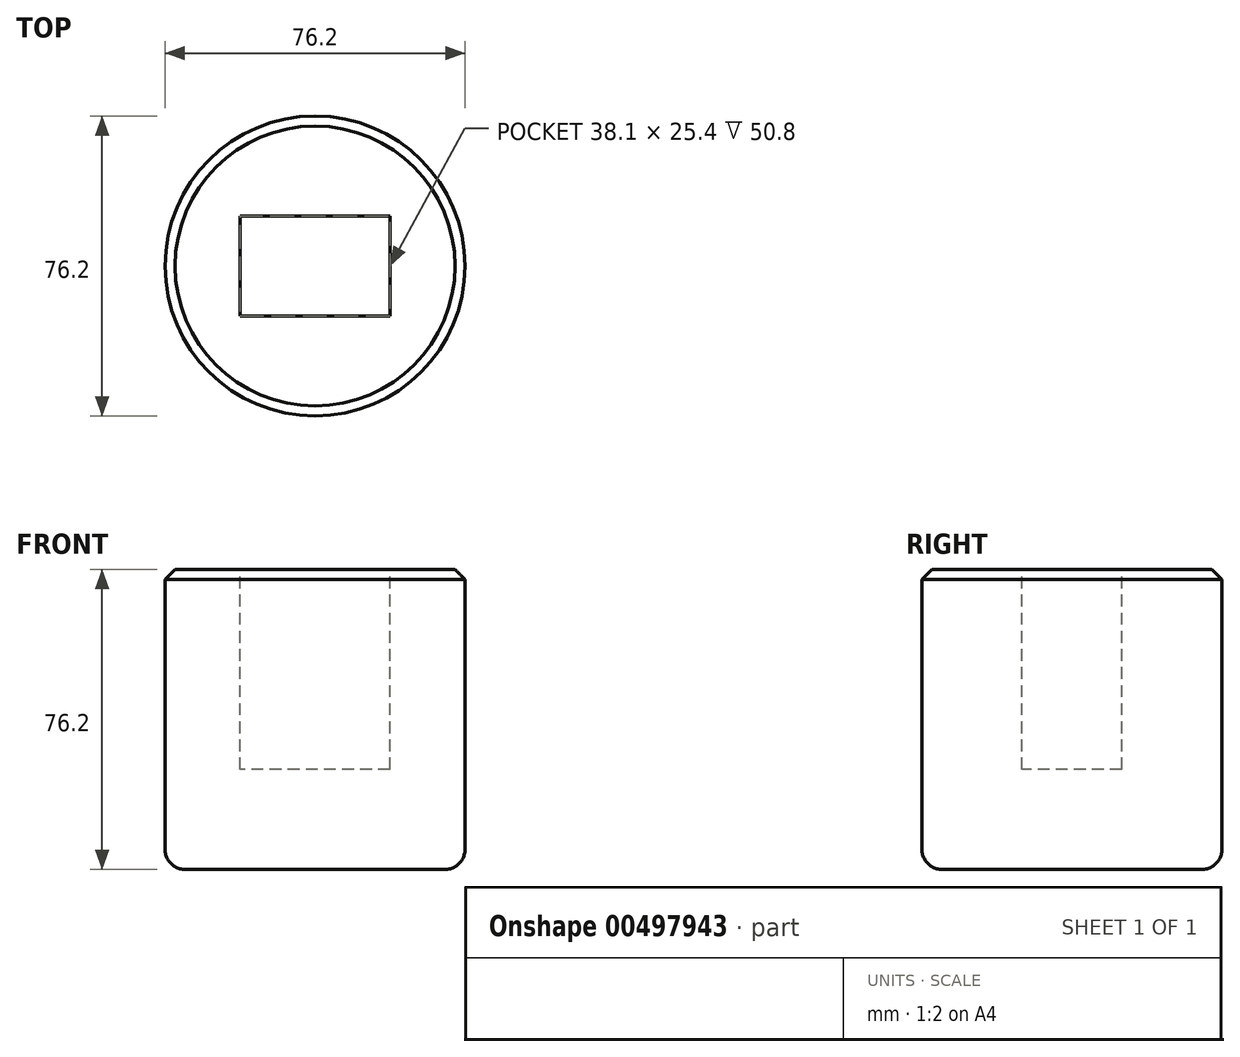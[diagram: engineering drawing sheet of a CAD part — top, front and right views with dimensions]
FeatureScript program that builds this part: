
annotation { "Feature Type Name" : "Feature", "Feature Type Description" : "" }
export const myFeature = defineFeature(function(context is Context, id is Id, definition is map)
    precondition{}
    {
        {
            var Q0;
            Q0=qCreatedBy(makeId("Top.planeOp"),FACE);
            var sketch = newSketch(context, id + "F0", { "sketchPlane" : qUnion([Q0])});
            skCircle(sketch, "E0", {"center": v(0, 0) * mm, "radius": 38.1 * mm});
            skSolve(sketch);
        }
        {
            var Q0;
            Q0 = qSketchRegion(id + "F0", true);
            extrude(context, id + "F1", {"entities" : qUnion([Q0]), "depth" : 76.2 * mm});
        }
        {
            var Q0;
            Q0=makeQuery(id+"F1.opExtrude","CAP_FACE",FACE,{"disambiguationData":[OSD([sQuery(id+"F0.wireOp",EDGE,"E0")])],"isStart":false});
            var sketch = newSketch(context, id + "F2", { "sketchPlane" : qUnion([Q0])});
            skLineSegment(sketch, "E1.bottom", {"start": v(19.05, 12.7) * mm, "end": v(-19.05, 12.7) * mm});
            skLineSegment(sketch, "E1.top", {"start": v(19.05, -12.7) * mm, "end": v(-19.05, -12.7) * mm});
            skLineSegment(sketch, "E1.left", {"start": v(19.05, 12.7) * mm, "end": v(19.05, -12.7) * mm});
            skLineSegment(sketch, "E1.right", {"start": v(-19.05, 12.7) * mm, "end": v(-19.05, -12.7) * mm});
            skPoint(sketch, "E1.middle", {"position": v(0, 0) * mm});
            skSolve(sketch);
        }
        {
            var Q0;
            Q0 = qSketchRegion(id + "F2", true);
            extrude(context, id + "F3", {"entities" : qUnion([Q0]), "operationType" : NewBodyOperationType.REMOVE, "oppositeDirection" : true, "depth" : 50.8 * mm});
        }
        {
            var Q0;
            Q0=makeQuery(id+"F1.opExtrude","CAP_EDGE",EDGE,{"disambiguationData":[OSD([sQuery(id+"F0.wireOp",EDGE,"E0")])],"isStart":false});
            chamfer(context, id + "F4", {"entities" : qUnion([Q0]), "width" : 2.54 * mm, "tangentPropagation" : true});
        }
        {
            var Q0;
            Q0=makeQuery(id+"F1.opExtrude","CAP_FACE",FACE,{"disambiguationData":[OSD([sQuery(id+"F0.wireOp",EDGE,"E0")])],"isStart":true});
            fillet(context, id + "F5", {"entities" : qUnion([Q0]), "radius" : 5.08 * mm, "tangentPropagation" : true, "allowEdgeOverflow" : false});
        }
    });
